# Revit family: lgh-n50_100rhw_rhp_60Hz
name_source: partatom
category: 機械設備
units: mm (PartAtom-declared; Revit-internal decimal feet)

## family parameters
OmniClass タイトル = Heat Exchangers for Ventilation Air
OmniClass 番号 = 23.75.10.34.21
パーツ タイプ = 標準
ロード時にボイドで切り取り = いいえ
丸型コネクタ寸法 = 直径を使用
作業面ベース = いいえ
共有 = いいえ
常に垂直 = はい
部屋計算ポイント = はい

## types (4) — shared parameters
Box_Depth = 136
Box_Height = 267  [stored 0.875984 ft]
Box_Width = 80
Clearance Right = 600
Duct_Depth = 79
IfcExportAs = IfcAirToAirHeatRecoveryType
IfcExportType = ROTARYWHEEL
OmniClassCode = 23-27 23 19 11
URL = https://www.mitsubishielectric.co.jp
Uniclass2015Code = Pr_60_60_36_88
Uniclass2015Title = Thermal wheels
Uniclass2015Version = Systems v1.9
ドレン皿_Height = 77
ドレン皿材質 = ABS樹脂
ドレン管_Depth = 28  [stored 0.0918635 ft]
ドレン管径 = 32 mm
メンテナンススペース = はい
仕様書バージョン = Version1.0
企業コード = 108420
初期抵抗 = 0.0 Pa
周波数 = 60 Hz
呼称 = 全熱交換ユニット
外気量 = 0.0 m³/h
天吊金具_幅 = 30  [stored 0.0984252 ft]
天吊金具_径 = 7  [stored 0.0229659 ft]
天吊金具_高さ = 7  [stored 0.0229659 ft]
実風量 = 0.0 m³/h
形式 = 天井埋込ダクト形
排気量 = 0.0 m³/h
有効加湿量 = 3.2
本体マテリアル = ポリエステル塗装鋼板
極数 = 2
法定耐用年数 = 15
消費電力_加湿器 = 0 W
温度交換効率 = 67.00%
点検口 = はい
点検口_Depth = 450  [stored 1.47638 ft]
点検口_Width = 450  [stored 1.47638 ft]
点検口離隔 = 150
相 = 1
積算_科目 = 1 空気調和設備
符号 = HEU
製品リリース年月 = 2013/7/1
製品出荷対象 = 国内
製造元 = 三菱電機株式会社
設置方法 = 天井吊(隠ぺい)形
設計風量 = 0.0 m³/h
説明 = 業務用ロスナイ 耐湿形
負荷分類 = 3_ファン類
運転質量 = 0.00 kg
電動機出力 = 0 W
電圧 = 100 V
zero-valued in all types: Clearance Bottom, Clearance Top, EAサイズ_W, OAサイズ_W, RAサイズ_W, SAサイズ_W

## per-type parameters (varying)
- LGH-N50RHP: Box_D=94  [stored 0.308399 ft]; Box_H=46; Depth=888  [stored 2.91339 ft]; Duct_Height=159; Duct_Pitch=745  [stored 2.44423 ft]; EAサイズ_D=192  [stored 0.629921 ft]; Height=317  [stored 1.04003 ft]; MAX静圧=150.0 Pa; MAX風量=500.0 m³/h; MIN静圧=40.0 Pa; MIN風量=260.0 m³/h; OAサイズ_D=192  [stored 0.629921 ft]; RAサイズ_D=192  [stored 0.629921 ft]; SAサイズ_D=192  [stored 0.629921 ft]; Width=1016; エンタルピ交換効率_冷房=0.00%; エンタルピ交換効率_暖房=0.00%; ドレン皿_Depth=934  [stored 3.0643 ft]; ドレン皿_Width=1183  [stored 3.88123 ft]; ドレン管_D=71; ドレン管_H=374  [stored 1.22703 ft]; 価格=345000 $; 分類コード=50054502100010; 天吊金具ピッチ1=1048; 天吊金具ピッチ2=790; 機外静圧=150.0 Pa; 機外静圧_排気=150.0 Pa; 消費電力=281 W; 点検口高さ=-317  [stored -1.04003 ft]; 製品質量=42.00 kg; 質量=50.40 kg; 面風速=4.4 m/s; 風量=500.0 m³/h; 騒音レベル(dB(A))=34
- LGH-N50RHW: Box_D=94  [stored 0.308399 ft]; Box_H=46; Depth=888  [stored 2.91339 ft]; Duct_Height=159; Duct_Pitch=745  [stored 2.44423 ft]; EAサイズ_D=192  [stored 0.629921 ft]; Height=317  [stored 1.04003 ft]; MAX静圧=150.0 Pa; MAX風量=500.0 m³/h; MIN静圧=40.0 Pa; MIN風量=260.0 m³/h; OAサイズ_D=192  [stored 0.629921 ft]; RAサイズ_D=192  [stored 0.629921 ft]; SAサイズ_D=192  [stored 0.629921 ft]; Width=1016; エンタルピ交換効率_冷房=46.00%; エンタルピ交換効率_暖房=53.00%; ドレン皿_Depth=934  [stored 3.0643 ft]; ドレン皿_Width=1183  [stored 3.88123 ft]; ドレン管_D=71; ドレン管_H=374  [stored 1.22703 ft]; 価格=376000 $; 分類コード=50052504100070; 天吊金具ピッチ1=1048; 天吊金具ピッチ2=790; 機外静圧=150.0 Pa; 機外静圧_排気=150.0 Pa; 消費電力=281 W; 点検口高さ=-317  [stored -1.04003 ft]; 製品質量=42.00 kg; 質量=50.40 kg; 面風速=4.4 m/s; 風量=500.0 m³/h; 騒音レベル(dB(A))=34
- LGH-N100RHP: Box_D=129; Box_H=127; Depth=1164; Duct_Height=199; Duct_Pitch=920; EAサイズ_D=242; Height=398; MAX静圧=180.0 Pa; MAX風量=1000.0 m³/h; MIN静圧=85.0 Pa; MIN風量=680.0 m³/h; OAサイズ_D=242; RAサイズ_D=242; SAサイズ_D=242; Width=1231; エンタルピ交換効率_冷房=0.00%; エンタルピ交換効率_暖房=0.00%; ドレン皿_Depth=1210; ドレン皿_Width=1398; ドレン管_D=90; ドレン管_H=455; 価格=653000 $; 分類コード=50054502100010; 天吊金具ピッチ1=1263; 天吊金具ピッチ2=1030; 機外静圧=180.0 Pa; 機外静圧_排気=180.0 Pa; 消費電力=630 W; 点検口高さ=-398; 製品質量=83.00 kg; 質量=99.60 kg; 面風速=5.7 m/s; 風量=1000.0 m³/h; 騒音レベル(dB(A))=37
- LGH-N100RHW: Box_D=129; Box_H=127; Depth=1164; Duct_Height=199; Duct_Pitch=920; EAサイズ_D=242; Height=398; MAX静圧=180.0 Pa; MAX風量=1000.0 m³/h; MIN静圧=85.0 Pa; MIN風量=680.0 m³/h; OAサイズ_D=242; RAサイズ_D=242; SAサイズ_D=242; Width=1231; エンタルピ交換効率_冷房=46.00%; エンタルピ交換効率_暖房=55.00%; ドレン皿_Depth=1210; ドレン皿_Width=1398; ドレン管_D=90; ドレン管_H=455; 価格=696000 $; 分類コード=50052504100070; 天吊金具ピッチ1=1263; 天吊金具ピッチ2=1030; 機外静圧=180.0 Pa; 機外静圧_排気=180.0 Pa; 消費電力=630 W; 点検口高さ=-398; 製品質量=83.00 kg; 質量=99.60 kg; 面風速=5.7 m/s; 風量=1000.0 m³/h; 騒音レベル(dB(A))=37

note: column(s) folded — value = type name in every type: モデル

note: [stored X ft] marks values corroborated as IEEE doubles in the binary element streams (Revit-internal decimal feet)

## geometry (parser evidence)
native form markers: Blend x2
no freeform markers — native parametric forms only
